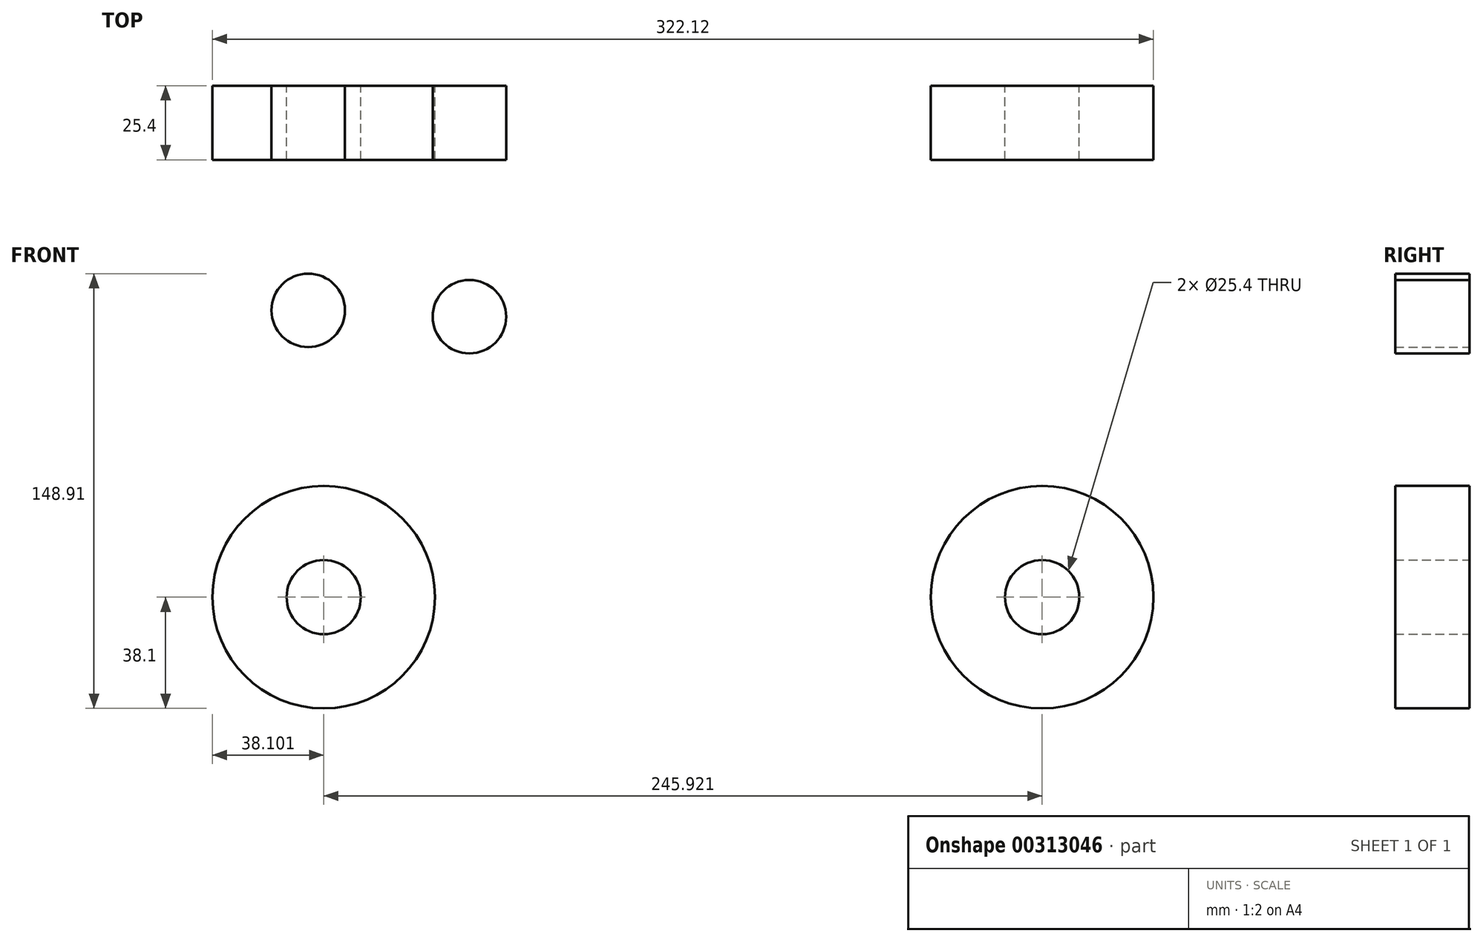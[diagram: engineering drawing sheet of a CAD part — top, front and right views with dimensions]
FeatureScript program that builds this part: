
annotation { "Feature Type Name" : "Feature", "Feature Type Description" : "" }
export const myFeature = defineFeature(function(context is Context, id is Id, definition is map)
    precondition{}
    {
        {
            var Q0;
            Q0=qCreatedBy(makeId("Front.planeOp"),FACE);
            var sketch = newSketch(context, id + "F0", { "sketchPlane" : qUnion([Q0])});
            skCircle(sketch, "E0", {"center": v(-156.8, 0) * mm, "radius": 38.1 * mm});
            skCircle(sketch, "E1", {"center": v(89.11, 0) * mm, "radius": 38.1 * mm});
            skCircle(sketch, "E2", {"center": v(-156.8, 0) * mm, "radius": 12.7 * mm});
            skCircle(sketch, "E3", {"center": v(89.11, 0) * mm, "radius": 12.7 * mm});
            skCircle(sketch, "E4", {"center": v(-162.1, 98.24) * mm, "radius": 12.57 * mm});
            skCircle(sketch, "E5", {"center": v(-106.95, 96.05) * mm, "radius": 12.57 * mm});
            skSolve(sketch);
        }
        {
            var Q0;
            Q0=makeQuery(id+"F0.imprint","IMPRINT",FACE,{"disambiguationData":[TD([[makeQuery(id+"F0.imprint","IMPRINT",EDGE,{"derivedFrom":sQuery(id+"F0.wireOp",EDGE,"E4")}),1.0]])]});
            var Q1;
            Q1=makeQuery(id+"F0.imprint","IMPRINT",FACE,{"disambiguationData":[TD([[makeQuery(id+"F0.imprint","IMPRINT",EDGE,{"derivedFrom":sQuery(id+"F0.wireOp",EDGE,"E5")}),1.0]])]});
            var Q2;
            Q2=makeQuery(id+"F0.imprint","IMPRINT",FACE,{"disambiguationData":[TD([[makeQuery(id+"F0.imprint","IMPRINT",EDGE,{"derivedFrom":sQuery(id+"F0.wireOp",EDGE,"E0")}),1.0]])]});
            var Q3;
            Q3=makeQuery(id+"F0.imprint","IMPRINT",FACE,{"disambiguationData":[TD([[makeQuery(id+"F0.imprint","IMPRINT",EDGE,{"derivedFrom":sQuery(id+"F0.wireOp",EDGE,"E1")}),1.0]])]});
            extrude(context, id + "F1", {"entities" : qUnion([Q0, Q1, Q2, Q3]), "depth" : 25.4 * mm});
        }
    });
